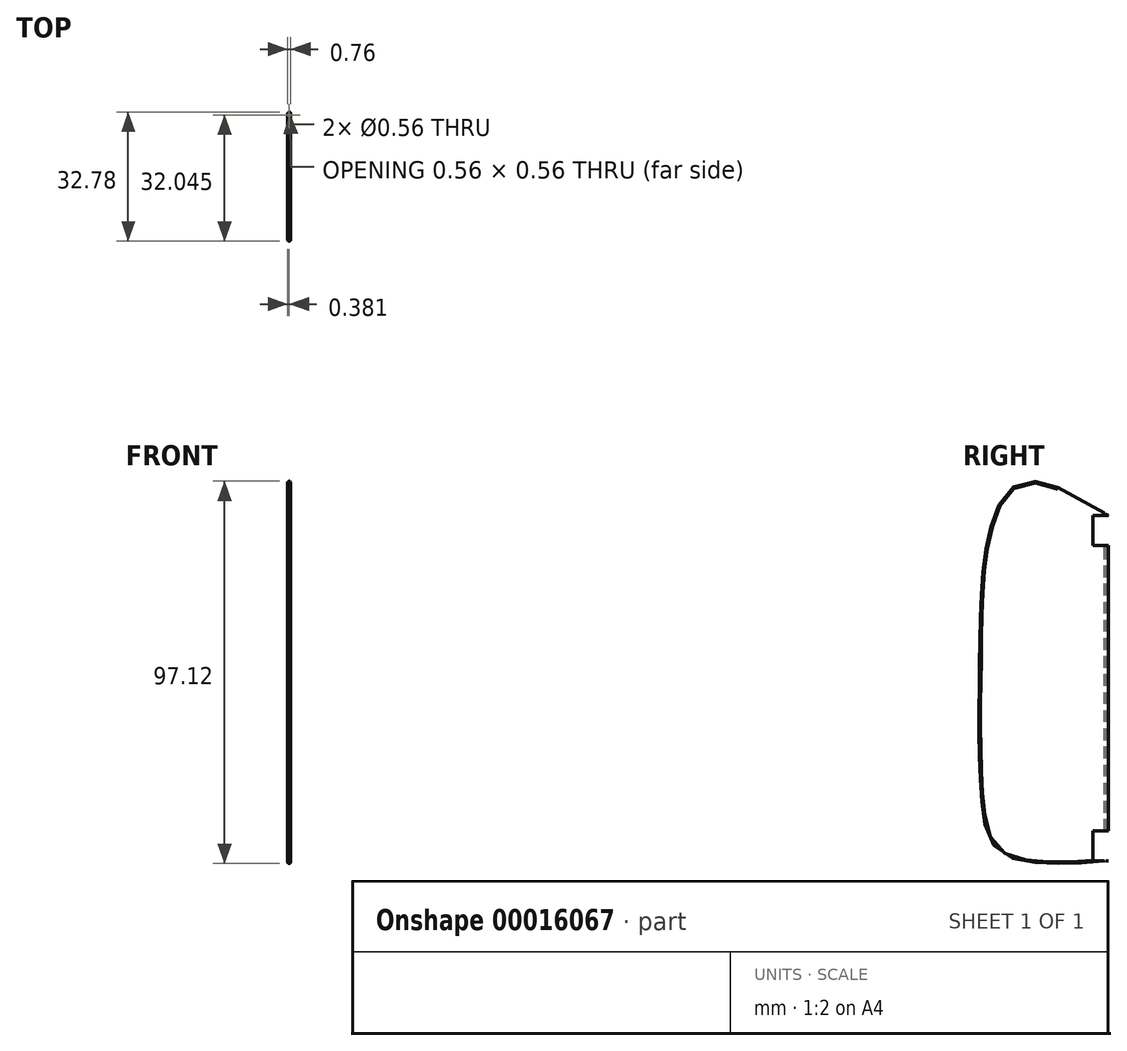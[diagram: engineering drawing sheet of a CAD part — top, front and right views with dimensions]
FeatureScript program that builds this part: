
annotation { "Feature Type Name" : "Feature", "Feature Type Description" : "" }
export const myFeature = defineFeature(function(context is Context, id is Id, definition is map)
    precondition{}
    {
        {
            var Q0;
            Q0=qCreatedBy(makeId("Right.planeOp"),FACE);
            var sketch = newSketch(context, id + "F0", { "sketchPlane" : qUnion([Q0])});
            skLineSegment(sketch, "E0", {"start": v(-11.09, 27.62) * mm, "end": v(-15, 27.62) * mm});
            skLineSegment(sketch, "E1", {"start": v(-15, 27.62) * mm, "end": v(-15, 20) * mm});
            skLineSegment(sketch, "E2", {"start": v(-15, 20) * mm, "end": v(-11.09, 20) * mm});
            skLineSegment(sketch, "E3", {"start": v(-11.09, 20) * mm, "end": v(-11.09, -52.54) * mm});
            skLineSegment(sketch, "E4", {"start": v(-11.09, -52.54) * mm, "end": v(-15, -52.54) * mm});
            skLineSegment(sketch, "E5", {"start": v(-15, -52.54) * mm, "end": v(-15, -60.16) * mm});
            skLineSegment(sketch, "E6", {"start": v(-15, -60.16) * mm, "end": v(-11.09, -60.16) * mm});
            skLineSegment(sketch, "E7", {"start": v(-11.09, 27.62) * mm, "end": v(-23.9, 34.63) * mm});
            skFitSpline(sketch, "E8", {"points": [v(-23.9, 34.63) * mm, v(-36, 34.2) * mm, v(-42.5, 16.48) * mm, v(-43.52, 0) * mm, v(-43.37, -42.82) * mm, v(-38.82, -57.66) * mm, v(-28.6, -60.69) * mm, v(-11.09, -60.16) * mm], "startDerivative": vector(-110.5, 56.29) * mm, "endDerivative": vector(176.24, 12.78) * mm});
            skSolve(sketch);
        }
        {
            var Q0;
            Q0=makeQuery(id+"F0.imprint","IMPRINT",FACE,{"disambiguationData":[TD([[makeQuery(id+"F0.imprint","IMPRINT",EDGE,{"derivedFrom":sQuery(id+"F0.wireOp",EDGE,"E0")}),-1.0]])]});
            extrude(context, id + "F1", {"entities" : qUnion([Q0]), "depth" : 0.76 * mm});
        }
        {
            var Q0;
            Q0=makeQuery(id+"F1.opExtrude","CAP_EDGE",EDGE,{"disambiguationData":[OSD([sQuery(id+"F0.wireOp",EDGE,"E8")])],"isStart":false});
            var Q1;
            Q1=makeQuery(id+"F1.opExtrude","CAP_EDGE",EDGE,{"disambiguationData":[OSD([sQuery(id+"F0.wireOp",EDGE,"E8")])],"isStart":true});
            fillet(context, id + "F2", {"entities" : qUnion([Q0, Q1]), "radius" : 0.38 * mm, "tangentPropagation" : true, "allowEdgeOverflow" : false});
        }
        {
            var Q0;
            Q0=makeQuery(id+"F1.opExtrude","CAP_EDGE",EDGE,{"disambiguationData":[OSD([sQuery(id+"F0.wireOp",EDGE,"E7")])],"isStart":false});
            var Q1;
            Q1=makeQuery(id+"F1.opExtrude","CAP_EDGE",EDGE,{"disambiguationData":[OSD([sQuery(id+"F0.wireOp",EDGE,"E7")])],"isStart":true});
            fillet(context, id + "F3", {"entities" : qUnion([Q0, Q1]), "radius" : 0.38 * mm, "allowEdgeOverflow" : false});
        }
        {
            var Q0;
            Q0=makeQuery(id+"F1.opExtrude","SWEPT_FACE",FACE,{"disambiguationData":[OSD([sQuery(id+"F0.wireOp",EDGE,"E2")])]});
            var sketch = newSketch(context, id + "F4", { "sketchPlane" : qUnion([Q0])});
            skCircle(sketch, "E9", {"center": v(0.38, -11.83) * mm, "radius": 0.28 * mm});
            skSolve(sketch);
        }
        {
            var Q0;
            Q0=makeQuery(id+"F4.imprint","IMPRINT",FACE,{"disambiguationData":[TD([[makeQuery(id+"F4.imprint","IMPRINT",EDGE,{"derivedFrom":sQuery(id+"F4.wireOp",EDGE,"E9")}),1.0]])]});
            extrude(context, id + "F5", {"entities" : qUnion([Q0]), "operationType" : NewBodyOperationType.REMOVE, "endBound" : BoundingType.SYMMETRIC, "oppositeDirection" : true, "depth" : 177.8 * mm});
        }
        {
            var Q0;
            Q0=makeQuery(id+"F1.opExtrude","CAP_EDGE",EDGE,{"disambiguationData":[OSD([sQuery(id+"F0.wireOp",EDGE,"E3")])],"isStart":false});
            var Q1;
            Q1=makeQuery(id+"F1.opExtrude","CAP_EDGE",EDGE,{"disambiguationData":[OSD([sQuery(id+"F0.wireOp",EDGE,"E3")])],"isStart":true});
            fillet(context, id + "F6", {"entities" : qUnion([Q0, Q1]), "radius" : 0.38 * mm, "tangentPropagation" : true, "allowEdgeOverflow" : false});
        }
    });
